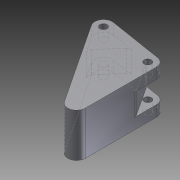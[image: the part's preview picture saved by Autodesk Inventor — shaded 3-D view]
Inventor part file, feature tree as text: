
AUTODESK INVENTOR PART (.ipt)
format: ipt  version: 2011 SP2 (Build 150309200, 309)  size: 133,632 bytes
history: native  units: mm
features: sketch x3, extrude x2, fillet x1, hole x1, projected_geometry x1
ambient origin geometry x8: Origin, YZ Plane, XZ Plane, XY Plane, X Axis, Y Axis, Z Axis, Center Point
bodies: Solid1 (feature_tree)
feature tree (8):
  extrude  "Extrusion1"  Depth=24.531041mm
  extrude  "Extrusion2"  Depth=4.0mm
  fillet  "Fillet1"  Radius=20.0mm
  hole  "Hole1"  [1 undecoded]
  sketch  "Sketch1"  dims[d0=32.752538mm d6=24.531041mm]
  sketch  "Sketch2"  dims[d14=43.915254mm d15=4.0mm d16=20.0mm d17=0.0mm]
  projected_geometry  "Projected Loop1"
  sketch  "Sketch3"  dims[d18=10.0mm d19=0.0mm d20=2.0mm d21=3.4mm d22=6.0mm d23=4.4mm d24=3.0mm d25=90.0deg d26=8.0mm d27=20.594885mm]
note: 1 required parameter value undecoded (feature->parameter linkage not recoverable at this tier; creation-order binding heuristic only, values carry confidence <= 0.55)
